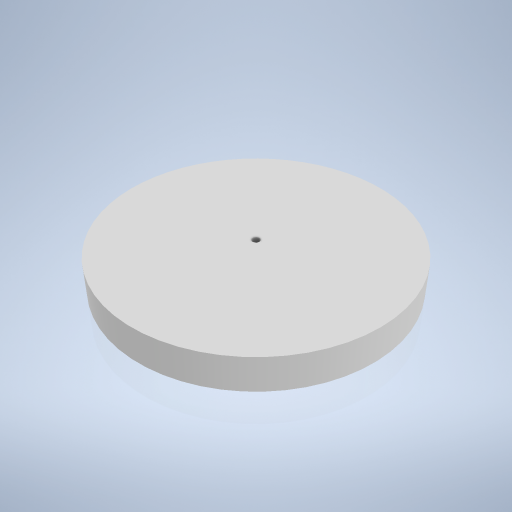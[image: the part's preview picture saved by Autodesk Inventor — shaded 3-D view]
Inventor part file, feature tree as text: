
AUTODESK INVENTOR PART (.ipt)
format: ipt  version: 2024.2 (Build 282272000, 272)  size: 214,528 bytes
history: native  units: mm
features: sketch x2, extrude x1, hole x1
ambient origin geometry x8: Origin, YZ Plane, XZ Plane, XY Plane, X Axis, Y Axis, Z Axis, Center Point
bodies: Volumenkörper1 (feature_tree)
feature tree (4):
  extrude  "Extrusion1"  Depth=6.0mm TaperAngle=0.0deg
  hole  "Bohrung1"  [1 undecoded]
  sketch  "Skizze1"  dims[d0=52.0mm d1=6.0mm d2=0.0mm]
  sketch  "Skizze2"  dims[d3=1.5mm d4=6.0mm d5=4.0mm d6=2.0mm d7=90.0deg d8=6.0mm d9=0.0mm]
note: 1 required parameter value undecoded (feature->parameter linkage not recoverable at this tier; creation-order binding heuristic only, values carry confidence <= 0.55)
